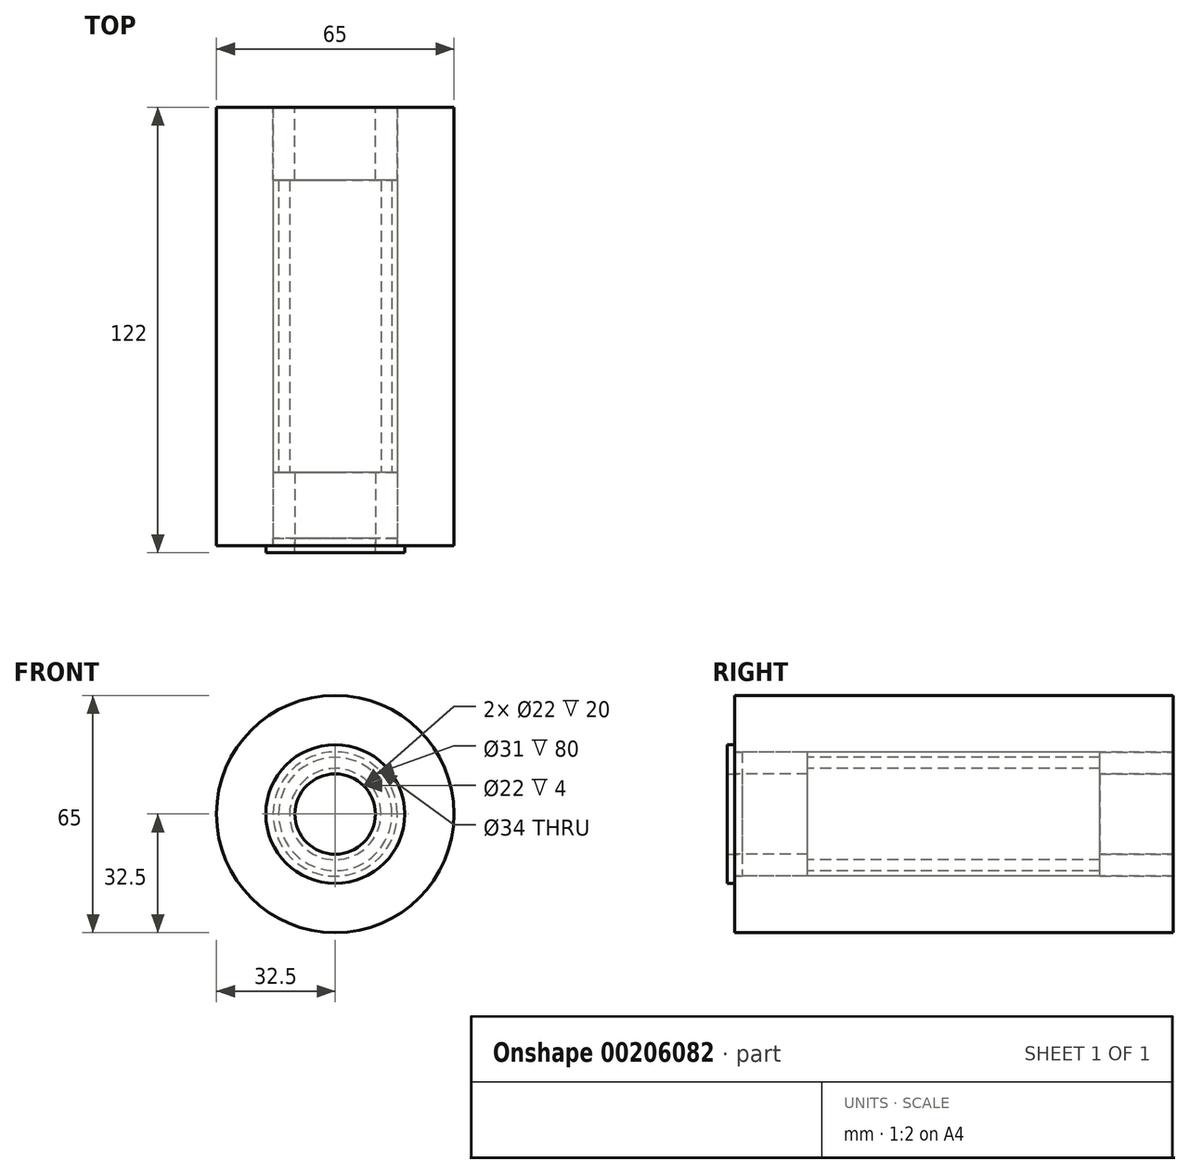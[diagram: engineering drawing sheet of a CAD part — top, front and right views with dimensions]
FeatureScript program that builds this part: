
annotation { "Feature Type Name" : "Feature", "Feature Type Description" : "" }
export const myFeature = defineFeature(function(context is Context, id is Id, definition is map)
    precondition{}
    {
        {
            var Q0;
            Q0=qCreatedBy(makeId("Front.planeOp"),FACE);
            var sketch = newSketch(context, id + "F0", { "sketchPlane" : qUnion([Q0])});
            skCircle(sketch, "E0", {"center": v(0, 0) * mm, "radius": 32.5 * mm});
            skCircle(sketch, "E1", {"center": v(0, 0) * mm, "radius": 17 * mm});
            skSolve(sketch);
        }
        {
            var Q0;
            Q0=makeQuery(id+"F0.imprint","IMPRINT",FACE,{"disambiguationData":[TD([[makeQuery(id+"F0.imprint","IMPRINT",EDGE,{"derivedFrom":sQuery(id+"F0.wireOp",EDGE,"E0")}),1.0]])]});
            extrude(context, id + "F1", {"entities" : qUnion([Q0]), "oppositeDirection" : true, "depth" : 120 * mm});
        }
        {
            var Q0;
            Q0=makeQuery(id+"F1.opExtrude","CAP_FACE",FACE,{"disambiguationData":[OSD([sQuery(id+"F0.wireOp",EDGE,"E0"),sQuery(id+"F0.wireOp",EDGE,"E1")])],"isStart":true});
            var sketch = newSketch(context, id + "F2", { "sketchPlane" : qUnion([Q0])});
            skCircle(sketch, "E2.0", {"center": v(0, 0) * mm, "radius": 17 * mm});
            skCircle(sketch, "E3", {"center": v(0, 0) * mm, "radius": 11 * mm});
            skSolve(sketch);
        }
        {
            var Q0;
            Q0=makeQuery(id+"F2.imprint","IMPRINT",FACE,{"disambiguationData":[TD([[makeQuery(id+"F2.imprint","IMPRINT",EDGE,{"derivedFrom":sQuery(id+"F2.wireOp",EDGE,"E2.0")}),1.0]])]});
            extrude(context, id + "F3", {"entities" : qUnion([Q0]), "oppositeDirection" : true, "depth" : 20 * mm});
        }
        {
            var Q0;
            Q0=makeQuery(id+"F1.opExtrude","CAP_FACE",FACE,{"disambiguationData":[OSD([sQuery(id+"F0.wireOp",EDGE,"E0"),sQuery(id+"F0.wireOp",EDGE,"E1")])],"isStart":false});
            var sketch = newSketch(context, id + "F4", { "sketchPlane" : qUnion([Q0])});
            skCircle(sketch, "E4.0", {"center": v(0, 0) * mm, "radius": 11 * mm});
            skCircle(sketch, "E5.0", {"center": v(0, 0) * mm, "radius": 17 * mm});
            skSolve(sketch);
        }
        {
            var Q0;
            Q0 = qSketchRegion(id + "F4", true);
            extrude(context, id + "F5", {"entities" : qUnion([Q0]), "oppositeDirection" : true, "depth" : 20 * mm});
        }
        {
            var Q0;
            Q0=qCreatedBy(makeId("Right.planeOp"),FACE);
            var sketch = newSketch(context, id + "F6", { "sketchPlane" : qUnion([Q0])});
            skLineSegment(sketch, "E6", {"start": v(-16.92, 0) * mm, "end": v(138.93, 0) * mm, "construction": true});
            skLineSegment(sketch, "E7", {"start": v(0, 0) * mm, "end": v(0, 11) * mm});
            skLineSegment(sketch, "E8", {"start": v(0, 11) * mm, "end": v(20, 11) * mm});
            skLineSegment(sketch, "E9", {"start": v(20, 11) * mm, "end": v(20, 12.5) * mm});
            skLineSegment(sketch, "E10", {"start": v(20, 12.5) * mm, "end": v(100, 12.5) * mm});
            skLineSegment(sketch, "E11", {"start": v(100, 12.5) * mm, "end": v(100, 11) * mm});
            skLineSegment(sketch, "E12", {"start": v(100, 11) * mm, "end": v(120, 11) * mm});
            skLineSegment(sketch, "E13", {"start": v(120, 11) * mm, "end": v(120, 0) * mm});
            skLineSegment(sketch, "E14", {"start": v(0, 0) * mm, "end": v(120, 0) * mm});
            skSolve(sketch);
        }
        {
            var Q0;
            Q0 = qSketchRegion(id + "F6", true);
            var Q1;
            Q1=sQuery(id+"F6.wireOp",EDGE,"E6");
            revolve(context, id + "F7", {"entities" : qUnion([Q0]), "axis" : qUnion([Q1]), "revolveType" : RevolveType.FULL});
        }
        {
            var Q0;
            Q0=qCreatedBy(makeId("Right.planeOp"),FACE);
            var sketch = newSketch(context, id + "F8", { "sketchPlane" : qUnion([Q0])});
            skLineSegment(sketch, "E15.bottom", {"start": v(20, 17) * mm, "end": v(100, 17) * mm});
            skLineSegment(sketch, "E15.top", {"start": v(20, 15.5) * mm, "end": v(100, 15.5) * mm});
            skLineSegment(sketch, "E15.left", {"start": v(20, 17) * mm, "end": v(20, 15.5) * mm});
            skLineSegment(sketch, "E15.right", {"start": v(100, 17) * mm, "end": v(100, 15.5) * mm});
            skLineSegment(sketch, "E16", {"start": v(0, 0) * mm, "end": v(133.31, 0) * mm, "construction": true});
            skSolve(sketch);
        }
        {
            var Q0;
            Q0=makeQuery(id+"F8.imprint","IMPRINT",FACE,{"disambiguationData":[TD([[makeQuery(id+"F8.imprint","IMPRINT",EDGE,{"derivedFrom":sQuery(id+"F8.wireOp",EDGE,"E15.bottom")}),-1.0]])]});
            var Q1;
            Q1=sQuery(id+"F8.wireOp",EDGE,"E16");
            revolve(context, id + "F9", {"entities" : qUnion([Q0]), "axis" : qUnion([Q1]), "revolveType" : RevolveType.FULL});
        }
        {
            var Q0;
            Q0=qCreatedBy(makeId("Right.planeOp"),FACE);
            var sketch = newSketch(context, id + "F10", { "sketchPlane" : qUnion([Q0])});
            skLineSegment(sketch, "E17", {"start": v(0, 19) * mm, "end": v(-2, 19) * mm});
            skLineSegment(sketch, "E18", {"start": v(-2, 19) * mm, "end": v(-2, 11) * mm});
            skLineSegment(sketch, "E19", {"start": v(-2, 11) * mm, "end": v(2, 11) * mm});
            skLineSegment(sketch, "E20", {"start": v(2, 11) * mm, "end": v(2, 17) * mm});
            skLineSegment(sketch, "E21", {"start": v(2, 17) * mm, "end": v(0, 17) * mm});
            skLineSegment(sketch, "E22", {"start": v(0, 17) * mm, "end": v(0, 19) * mm});
            skLineSegment(sketch, "E23", {"start": v(0, 0) * mm, "end": v(-31.67, 0) * mm, "construction": true});
            skSolve(sketch);
        }
        {
            var Q0;
            Q0=makeQuery(id+"F10.imprint","IMPRINT",FACE,{"disambiguationData":[TD([[makeQuery(id+"F10.imprint","IMPRINT",EDGE,{"derivedFrom":sQuery(id+"F10.wireOp",EDGE,"E17")}),1.0]])]});
            var Q1;
            Q1=sQuery(id+"F10.wireOp",EDGE,"E23");
            revolve(context, id + "F11", {"entities" : qUnion([Q0]), "axis" : qUnion([Q1]), "revolveType" : RevolveType.FULL});
        }
    });
